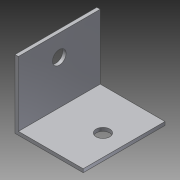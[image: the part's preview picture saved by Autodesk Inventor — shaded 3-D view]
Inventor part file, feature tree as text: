
AUTODESK INVENTOR PART (.ipt)
format: ipt  version: 2014 SP1 (Build 180222100, 222)  size: 100,352 bytes
history: native  units: in
note: dims shown in document units (in); Inventor stores cm internally (conversion verified against a paired STEP export)
features: extrude x3, sketch x3, plane x1
ambient origin geometry x8: Origin, YZ Plane, XZ Plane, XY Plane, X Axis, Y Axis, Z Axis, Center Point
bodies: Solid1 (feature_tree)
feature tree (7):
  extrude  "Extrusion1"  Depth=0.0312in
  sketch  "Sketch2"  dims[d2=0.75in d3=0.0in d4=0.125in]
  sketch  "Sketch3"  dims[d5=0.125in d6=0.75in d7=0.0in d8=0.75in d9=0.0in d10=0.4in d11=0.625in d12=0.5938in d13=0.4in]
  extrude  "Extrusion2"  Depth=0.75in
  extrude  "Extrusion3"  Depth=0.75in TaperAngle=0.0deg
  plane  "Work Plane1"
  sketch  "Sketch1"  dims[d0=0.625in d1=0.0312in]
